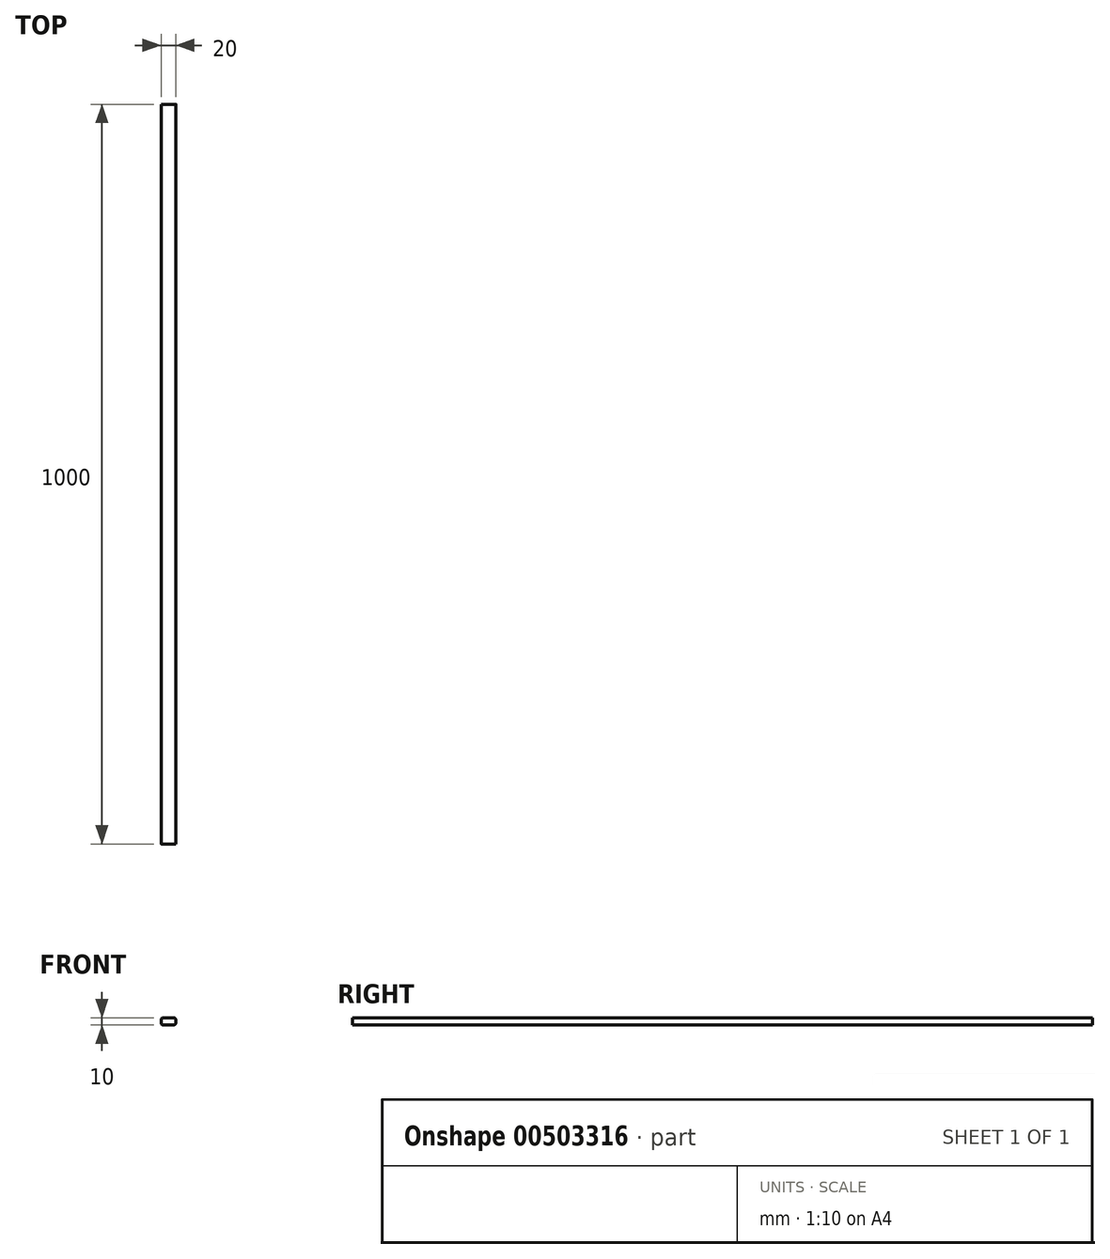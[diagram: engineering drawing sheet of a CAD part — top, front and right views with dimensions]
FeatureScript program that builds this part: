
annotation { "Feature Type Name" : "Feature", "Feature Type Description" : "" }
export const myFeature = defineFeature(function(context is Context, id is Id, definition is map)
    precondition{}
    {
        {
            var Q0;
            Q0=qCreatedBy(makeId("Front.planeOp"),FACE);
            var sketch = newSketch(context, id + "F0", { "sketchPlane" : qUnion([Q0])});
            skLineSegment(sketch, "E0.bottom", {"start": v(6.83, 5) * mm, "end": v(-6.83, 5) * mm});
            skLineSegment(sketch, "E0.top", {"start": v(6.83, -5) * mm, "end": v(-6.83, -5) * mm});
            skLineSegment(sketch, "E0.left", {"start": v(10, 1.83) * mm, "end": v(10, -1.83) * mm});
            skLineSegment(sketch, "E0.right", {"start": v(-10, 1.83) * mm, "end": v(-10, -1.83) * mm});
            skPoint(sketch, "E0.middle", {"position": v(0, 0) * mm});
            skPoint(sketch, "E1.visualSharp", {"position": v(-10, 5) * mm});
            skArc(sketch, "E1.filletArc", {"start": v(-6.83, 5) * mm, "mid": v(-9.07, 4.07) * mm, "end": v(-10, 1.83) * mm});
            skPoint(sketch, "E2.visualSharp", {"position": v(10, 5) * mm});
            skArc(sketch, "E2.filletArc", {"start": v(10, 1.83) * mm, "mid": v(9.07, 4.07) * mm, "end": v(6.83, 5) * mm});
            skPoint(sketch, "E3.visualSharp", {"position": v(10, -5) * mm});
            skArc(sketch, "E3.filletArc", {"start": v(6.83, -5) * mm, "mid": v(9.07, -4.07) * mm, "end": v(10, -1.83) * mm});
            skPoint(sketch, "E4.visualSharp", {"position": v(-10, -5) * mm});
            skArc(sketch, "E4.filletArc", {"start": v(-10, -1.83) * mm, "mid": v(-9.07, -4.07) * mm, "end": v(-6.83, -5) * mm});
            skLineSegment(sketch, "E5", {"start": v(-10, 1) * mm, "end": v(10, 1) * mm, "construction": true});
            skSolve(sketch);
        }
        {
            var Q0;
            Q0 = qSketchRegion(id + "F0", true);
            extrude(context, id + "F1", {"entities" : qUnion([Q0]), "depth" : 1000 * mm});
        }
    });
